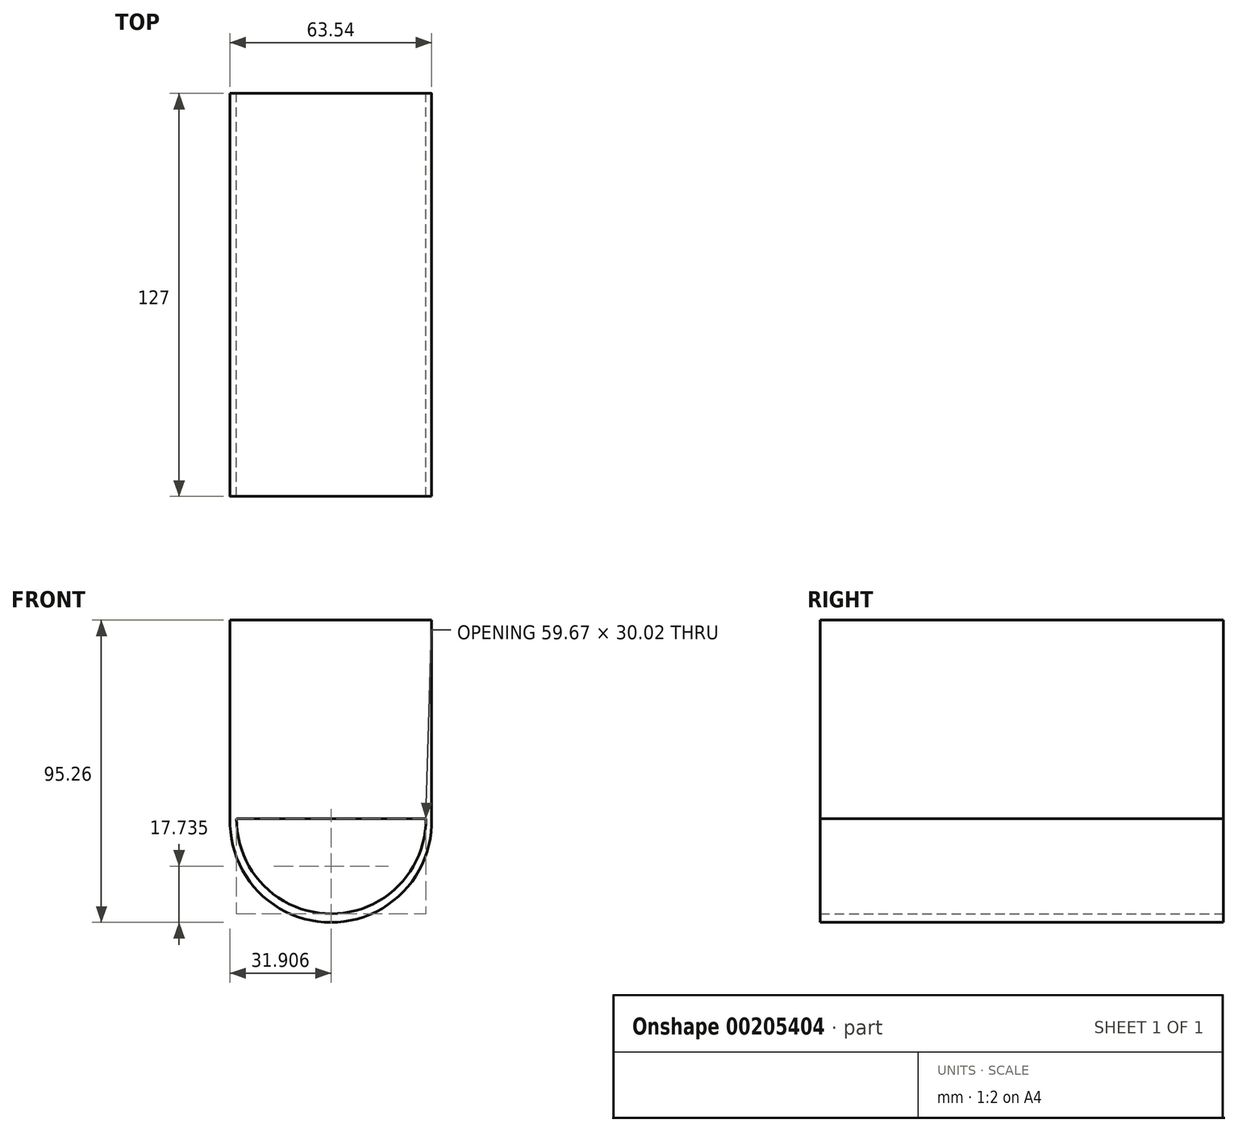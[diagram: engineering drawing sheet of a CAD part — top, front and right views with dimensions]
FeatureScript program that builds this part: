
annotation { "Feature Type Name" : "Feature", "Feature Type Description" : "" }
export const myFeature = defineFeature(function(context is Context, id is Id, definition is map)
    precondition{}
    {
        {
            var Q0;
            Q0=qCreatedBy(makeId("Front.planeOp"),FACE);
            var sketch = newSketch(context, id + "F0", { "sketchPlane" : qUnion([Q0])});
            skLineSegment(sketch, "E0.bottom", {"start": v(-31.75, 31.75) * mm, "end": v(31.75, 31.75) * mm});
            skLineSegment(sketch, "E0.top", {"start": v(-31.75, -31.75) * mm, "end": v(31.75, -31.75) * mm});
            skLineSegment(sketch, "E0.left", {"start": v(-31.75, 31.75) * mm, "end": v(-31.75, -31.75) * mm});
            skLineSegment(sketch, "E0.right", {"start": v(31.75, 31.75) * mm, "end": v(31.75, -31.75) * mm});
            skPoint(sketch, "E0.middle", {"position": v(0, 0) * mm});
            skSolve(sketch);
        }
        {
            var Q0;
            Q0 = qSketchRegion(id + "F0", true);
            extrude(context, id + "F1", {"entities" : qUnion([Q0]), "depth" : 127 * mm});
        }
        {
            var Q0;
            Q0=qCreatedBy(makeId("Front.planeOp"),FACE);
            var sketch = newSketch(context, id + "F2", { "sketchPlane" : qUnion([Q0])});
            skCircle(sketch, "E1", {"center": v(0, -31.75) * mm, "radius": 31.77 * mm});
            skSolve(sketch);
        }
        {
            var Q0;
            Q0 = qSketchRegion(id + "F2", true);
            extrude(context, id + "F3", {"entities" : qUnion([Q0]), "operationType" : NewBodyOperationType.ADD, "depth" : 127 * mm});
        }
        {
            var Q0;
            Q0=makeQuery(id+"F3.boolean.opBoolean","MERGE",FACE,{"derivedFrom":[makeQuery(id+"F1.opExtrude","CAP_FACE",FACE,{"disambiguationData":[OSD([sQuery(id+"F0.wireOp",EDGE,"E0.bottom"),sQuery(id+"F0.wireOp",EDGE,"E0.top"),sQuery(id+"F0.wireOp",EDGE,"E0.left"),sQuery(id+"F0.wireOp",EDGE,"E0.right")])],"isStart":true}),makeQuery(id+"F3.opExtrude","CAP_FACE",FACE,{"disambiguationData":[OSD([sQuery(id+"F2.wireOp",EDGE,"E1")])],"isStart":true})]});
            var sketch = newSketch(context, id + "F4", { "sketchPlane" : qUnion([Q0])});
            skLineSegment(sketch, "E2", {"start": v(-29.97, -30.76) * mm, "end": v(29.7, -30.76) * mm});
            skArc(sketch, "E3", {"start": v(-29.97, -30.76) * mm, "mid": v(-0.14, -60.79) * mm, "end": v(29.7, -30.76) * mm});
            skSolve(sketch);
        }
        {
            var Q0;
            Q0=makeQuery(id+"F4.imprint","IMPRINT",FACE,{"disambiguationData":[TD([[makeQuery(id+"F4.imprint","IMPRINT",EDGE,{"derivedFrom":sQuery(id+"F4.wireOp",EDGE,"E2")}),-1.0]])]});
            extrude(context, id + "F5", {"entities" : qUnion([Q0]), "operationType" : NewBodyOperationType.REMOVE, "oppositeDirection" : true, "depth" : 152.4 * mm});
        }
    });
